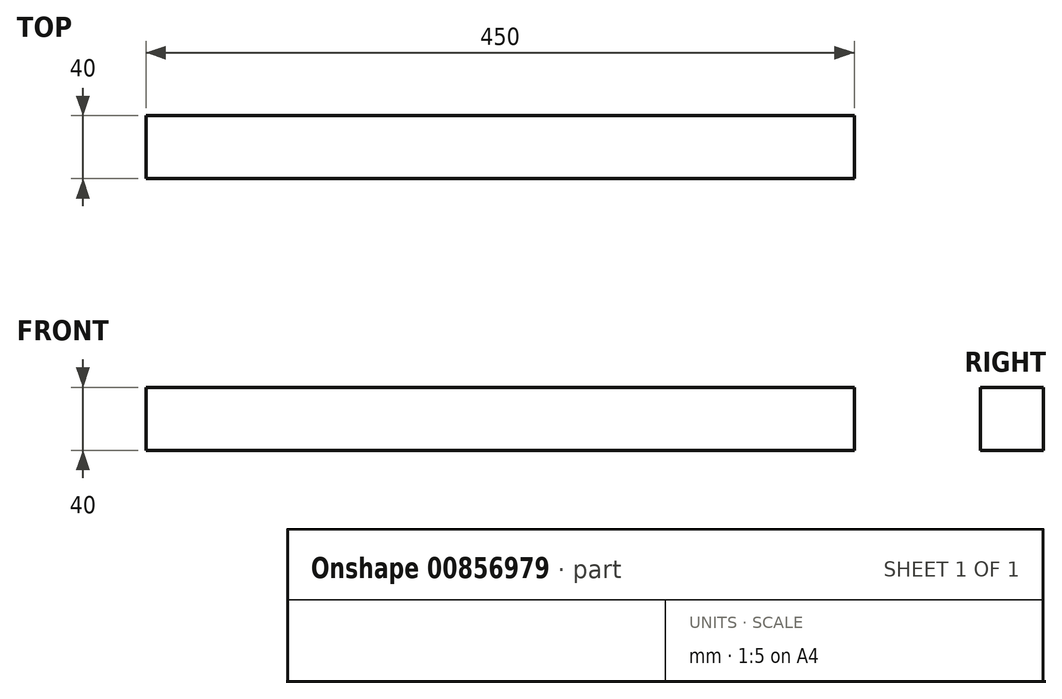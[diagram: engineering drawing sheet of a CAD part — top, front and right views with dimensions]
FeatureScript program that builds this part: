
annotation { "Feature Type Name" : "Feature", "Feature Type Description" : "" }
export const myFeature = defineFeature(function(context is Context, id is Id, definition is map)
    precondition{}
    {
        {
            var Q0;
            Q0=qCreatedBy(makeId("Right.planeOp"),FACE);
            var sketch = newSketch(context, id + "F0", { "sketchPlane" : qUnion([Q0])});
            skLineSegment(sketch, "E0.bottom", {"start": v(0, 0) * mm, "end": v(40, 0) * mm});
            skLineSegment(sketch, "E0.top", {"start": v(0, -40) * mm, "end": v(40, -40) * mm});
            skLineSegment(sketch, "E0.left", {"start": v(0, 0) * mm, "end": v(0, -40) * mm});
            skLineSegment(sketch, "E0.right", {"start": v(40, 0) * mm, "end": v(40, -40) * mm});
            skSolve(sketch);
        }
        {
            var Q0;
            Q0=makeQuery(id+"F0.imprint","IMPRINT",FACE,{"disambiguationData":[TD([[makeQuery(id+"F0.imprint","IMPRINT",EDGE,{"derivedFrom":sQuery(id+"F0.wireOp",EDGE,"E0.bottom")}),-1.0]])]});
            extrude(context, id + "F1", {"entities" : qUnion([Q0]), "depth" : 450 * mm, "offsetDistance" : 25 * mm});
        }
    });
